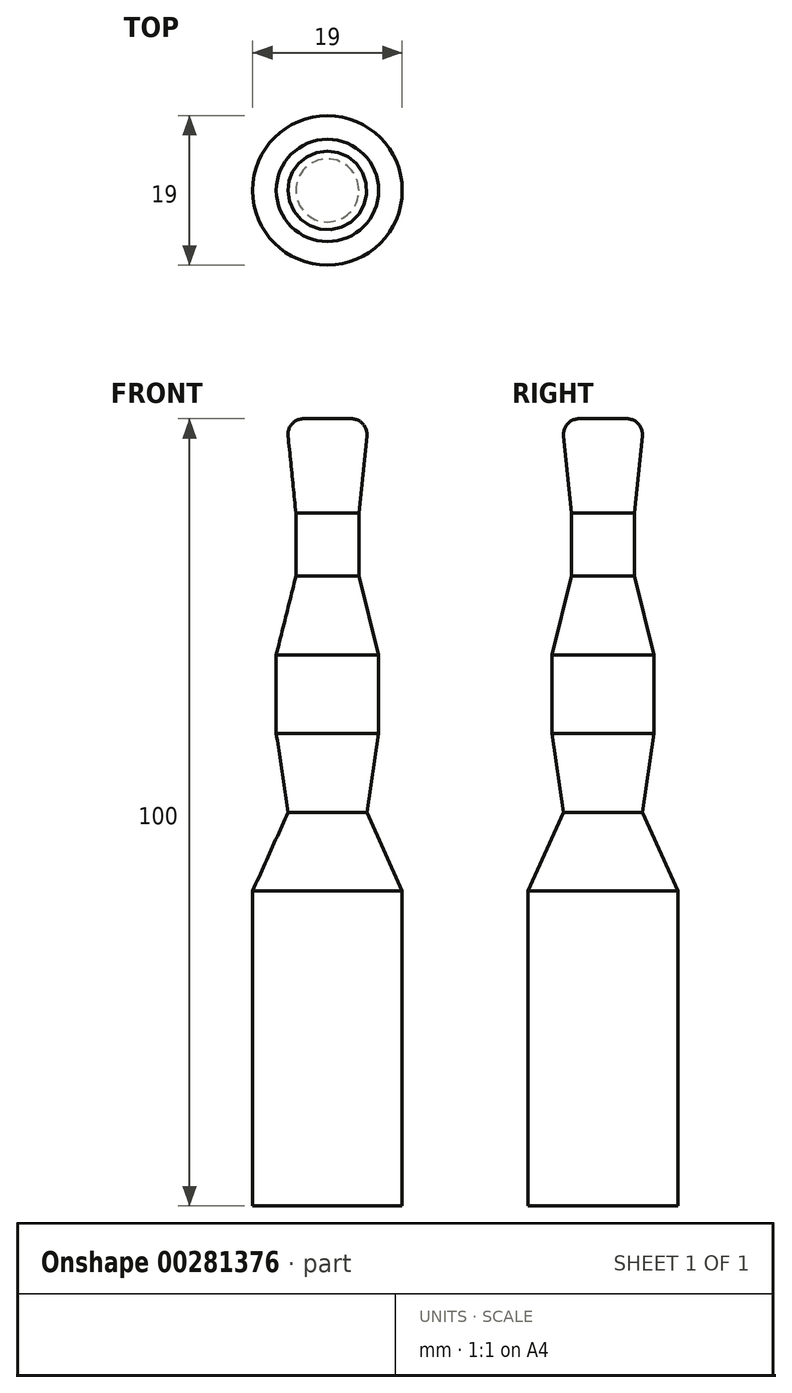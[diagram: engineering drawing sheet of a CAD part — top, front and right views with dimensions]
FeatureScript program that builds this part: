
annotation { "Feature Type Name" : "Feature", "Feature Type Description" : "" }
export const myFeature = defineFeature(function(context is Context, id is Id, definition is map)
    precondition{}
    {
        {
            var Q0;
            Q0=qCreatedBy(makeId("Front.planeOp"),FACE);
            var sketch = newSketch(context, id + "F0", { "sketchPlane" : qUnion([Q0])});
            skLineSegment(sketch, "E0", {"start": v(0, 0) * mm, "end": v(3.01, 0) * mm});
            skLineSegment(sketch, "E1", {"start": v(5, -2.2) * mm, "end": v(4, -12) * mm});
            skLineSegment(sketch, "E2", {"start": v(4, -12) * mm, "end": v(4, -20) * mm});
            skLineSegment(sketch, "E3", {"start": v(4, -20) * mm, "end": v(6.5, -30) * mm});
            skLineSegment(sketch, "E4", {"start": v(6.5, -30) * mm, "end": v(6.5, -40) * mm});
            skLineSegment(sketch, "E5", {"start": v(6.5, -40) * mm, "end": v(5, -50) * mm});
            skLineSegment(sketch, "E6", {"start": v(5, -50) * mm, "end": v(9.5, -60) * mm});
            skLineSegment(sketch, "E7", {"start": v(9.5, -60) * mm, "end": v(9.5, -100) * mm});
            skLineSegment(sketch, "E8", {"start": v(9.5, -100) * mm, "end": v(0, -100) * mm});
            skLineSegment(sketch, "E9", {"start": v(0, -100) * mm, "end": v(0, 0) * mm});
            skPoint(sketch, "E10.visualSharp", {"position": v(5.22, 0) * mm});
            skArc(sketch, "E10.filletArc", {"start": v(5, -2.2) * mm, "mid": v(4.5, -0.66) * mm, "end": v(3.01, 0) * mm});
            skSolve(sketch);
        }
        {
            var Q0;
            Q0 = qSketchRegion(id + "F0", true);
            var Q1;
            Q1=sQuery(id+"F0.wireOp",EDGE,"E9");
            revolve(context, id + "F1", {"entities" : qUnion([Q0]), "axis" : qUnion([Q1]), "revolveType" : RevolveType.FULL});
        }
    });
